# Revit family: 2120240 - Waste Bin NOX605
name_source: partatom
category: Specialty Equipment
units: mm (PartAtom-declared; Revit-internal decimal feet)

## family parameters
Always vertical = Yes
Cut with Voids When Loaded = No
OmniClass Number = 23.40.20.21.17
OmniClass Title = Paper Towel Dispensers, Disposal Units
Part Type = Normal
Room Calculation Point = No
Round Connector Dimension = Use Diameter
Shared = No
Work Plane-Based = No

## types (1)
- Waste Bin NOX605
    Assembly Code = C1030200
    Default Elevation = 0 mm  [stored 0 ft]
    Dimension = 355mm x 460mm x 168mm
    Manufacturer = Franke South Africa (Pty) Ltd
    Material = Grade 304 18/10, satin finish
    Model = Waste Bin NOX605
Sanitary Towel Dispenser and Waste Bin RODX611
Sanitary Towel Dispenser and Waste Bin RODX611
Sanitary Towel Dispenser and Waste Bin RODX611
    Product Code = 2120240

note: [stored X ft] marks values corroborated as IEEE doubles in the binary element streams (Revit-internal decimal feet)

## geometry (parser evidence)
native form markers: Blend x4, Sweep x3
no freeform markers — native parametric forms only
